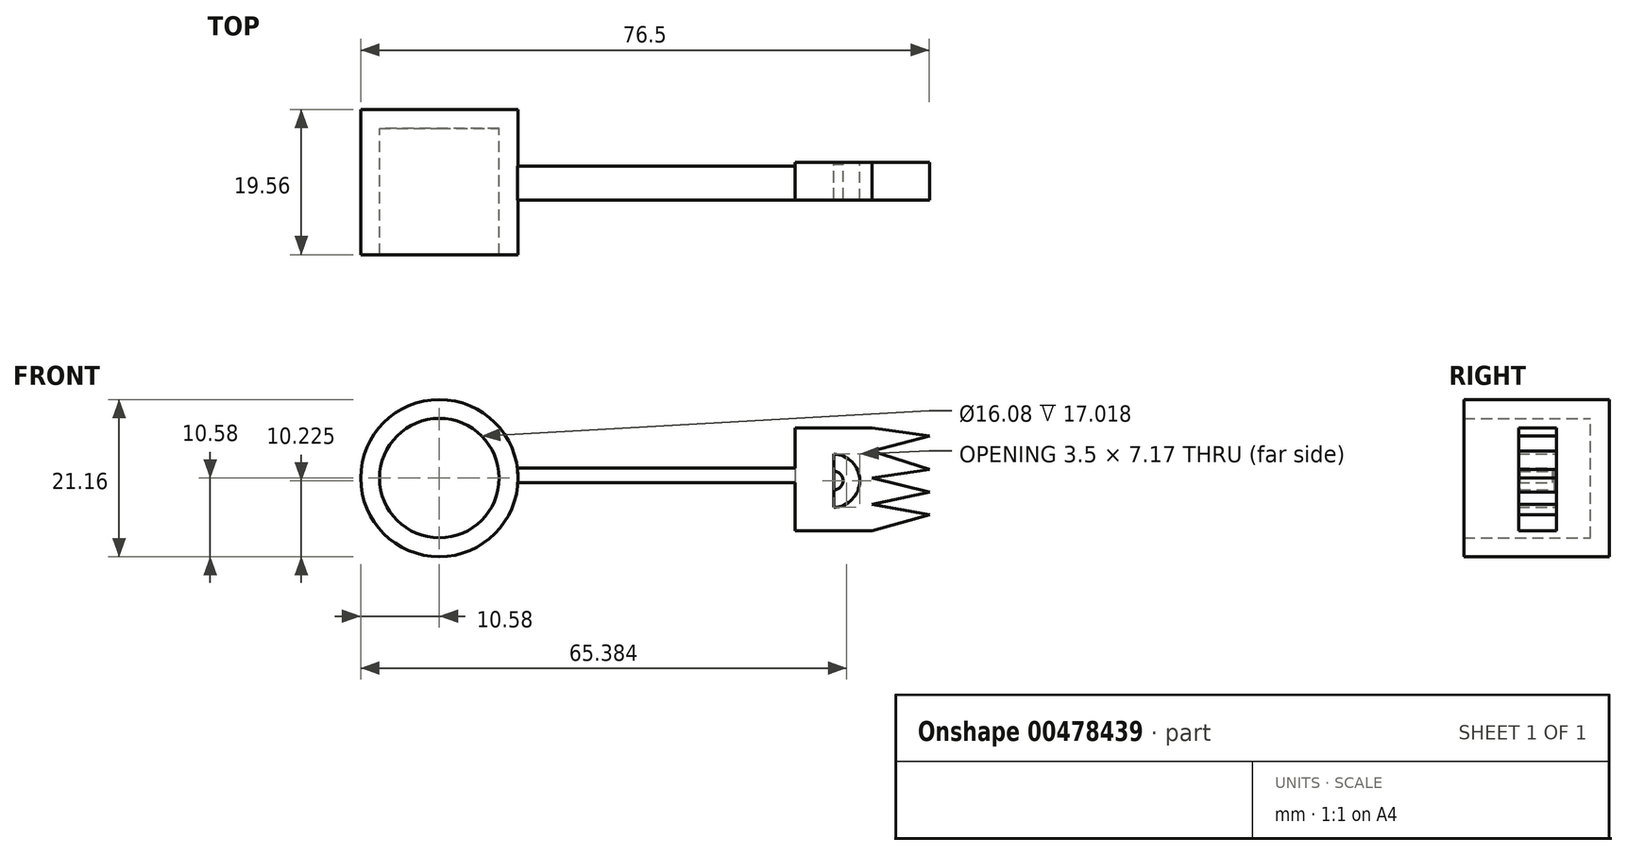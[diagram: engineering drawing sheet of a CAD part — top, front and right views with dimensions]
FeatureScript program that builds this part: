
annotation { "Feature Type Name" : "Feature", "Feature Type Description" : "" }
export const myFeature = defineFeature(function(context is Context, id is Id, definition is map)
    precondition{}
    {
        {
            var Q0;
            Q0=qCreatedBy(makeId("Front.planeOp"),FACE);
            var sketch = newSketch(context, id + "F0", { "sketchPlane" : qUnion([Q0])});
            skCircle(sketch, "E0", {"center": v(0, 0) * mm, "radius": 10.58 * mm});
            skLineSegment(sketch, "E1", {"start": v(10.5, 1.34) * mm, "end": v(47.87, 1.34) * mm});
            skLineSegment(sketch, "E2", {"start": v(47.87, 1.34) * mm, "end": v(47.87, -0.63) * mm});
            skLineSegment(sketch, "E3", {"start": v(47.87, -0.63) * mm, "end": v(10.56, -0.63) * mm});
            skLineSegment(sketch, "E4", {"start": v(10.56, -0.63) * mm, "end": v(10.5, 1.34) * mm});
            skLineSegment(sketch, "E5", {"start": v(47.87, 6.75) * mm, "end": v(47.87, -7.1) * mm});
            skLineSegment(sketch, "E6", {"start": v(47.87, 6.75) * mm, "end": v(58.24, 6.75) * mm});
            skLineSegment(sketch, "E7", {"start": v(58.24, -7.1) * mm, "end": v(47.87, -7.1) * mm});
            skLineSegment(sketch, "E8", {"start": v(58.24, 6.75) * mm, "end": v(65.92, 5.7) * mm});
            skLineSegment(sketch, "E9", {"start": v(65.92, 5.7) * mm, "end": v(58.24, 3.62) * mm});
            skLineSegment(sketch, "E10", {"start": v(58.24, 3.62) * mm, "end": v(65.92, 1.15) * mm});
            skLineSegment(sketch, "E11", {"start": v(65.92, 1.15) * mm, "end": v(58.24, 0) * mm});
            skLineSegment(sketch, "E12", {"start": v(58.24, 0) * mm, "end": v(65.92, -1.89) * mm});
            skLineSegment(sketch, "E13", {"start": v(65.92, -1.89) * mm, "end": v(58.24, -3.5) * mm});
            skLineSegment(sketch, "E14", {"start": v(58.24, -3.5) * mm, "end": v(65.92, -4.93) * mm});
            skLineSegment(sketch, "E15", {"start": v(65.92, -4.93) * mm, "end": v(58.24, -7.1) * mm});
            skArc(sketch, "E16", {"start": v(53.06, -3.94) * mm, "mid": v(56.55, -0.36) * mm, "end": v(53.06, 3.23) * mm});
            skPoint(sketch, "E16.startSnap0", {"position": v(53.06, 6.75) * mm});
            skPoint(sketch, "E16.endSnap0", {"position": v(53.06, 6.75) * mm});
            skLineSegment(sketch, "E17", {"start": v(53.06, 3.23) * mm, "end": v(53.06, 0.93) * mm});
            skLineSegment(sketch, "E18", {"start": v(53.06, -3.94) * mm, "end": v(53.06, -1.59) * mm});
            skArc(sketch, "E19", {"start": v(53.06, -1.59) * mm, "mid": v(54.32, -0.33) * mm, "end": v(53.06, 0.93) * mm});
            skLineSegment(sketch, "E20", {"start": v(53.06, 0.93) * mm, "end": v(53.06, -1.59) * mm});
            skSolve(sketch);
        }
        {
            var Q0;
            Q0=makeQuery(id+"F0.imprint","IMPRINT",FACE,{"disambiguationData":[TD([[makeQuery(id+"F0.imprint","IMPRINT",EDGE,{"derivedFrom":sQuery(id+"F0.wireOp",EDGE,"E0")}),1.0]])]});
            extrude(context, id + "F1", {"entities" : qUnion([Q0]), "depth" : 19.56 * mm});
        }
        {
            var Q0;
            Q0=makeQuery(id+"F1.opExtrude","CAP_FACE",FACE,{"disambiguationData":[OSD([sQuery(id+"F0.wireOp",EDGE,"E0")])],"isStart":false});
            shell(context, id + "F2", {"entities" : qUnion([Q0]), "thickness" : 2.54 * mm});
        }
        {
            var Q0;
            {var subQ1=sQuery(id+"F0.wireOp",EDGE,"E1");Q0=makeQuery(id+"F0.imprint","IMPRINT",FACE,{"disambiguationData":[TD([[makeQuery(id+"F0.imprint","IMPRINT",EDGE,{"derivedFrom":subQ1}),-1.0]])]});}
            extrude(context, id + "F3", {"entities" : qUnion([Q0]), "operationType" : NewBodyOperationType.ADD, "depth" : 12.2 * mm, "hasSecondDirection" : true, "secondDirectionOppositeDirection" : false, "secondDirectionDepth" : 7.62 * mm});
        }
        {
            var Q0;
            {var subQ3=sQuery(id+"F0.wireOp",EDGE,"E6");Q0=makeQuery(id+"F0.imprint","IMPRINT",FACE,{"disambiguationData":[TD([[makeQuery(id+"F0.imprint","IMPRINT",EDGE,{"derivedFrom":subQ3}),-1.0]])]});}
            extrude(context, id + "F4", {"entities" : qUnion([Q0]), "operationType" : NewBodyOperationType.ADD, "depth" : 12.2 * mm, "hasSecondDirection" : true, "secondDirectionOppositeDirection" : false, "secondDirectionDepth" : 7.11 * mm});
        }
        {
            var Q0;
            Q0=makeQuery(id+"F0.imprint","IMPRINT",FACE,{"disambiguationData":[TD([[makeQuery(id+"F0.imprint","IMPRINT",EDGE,{"derivedFrom":sQuery(id+"F0.wireOp",EDGE,"E19")}),1.0]])]});
            extrude(context, id + "F5", {"entities" : qUnion([Q0]), "operationType" : NewBodyOperationType.ADD, "depth" : 12.06 * mm, "hasSecondDirection" : true, "secondDirectionOppositeDirection" : false, "secondDirectionDepth" : 7.37 * mm});
        }
    });
